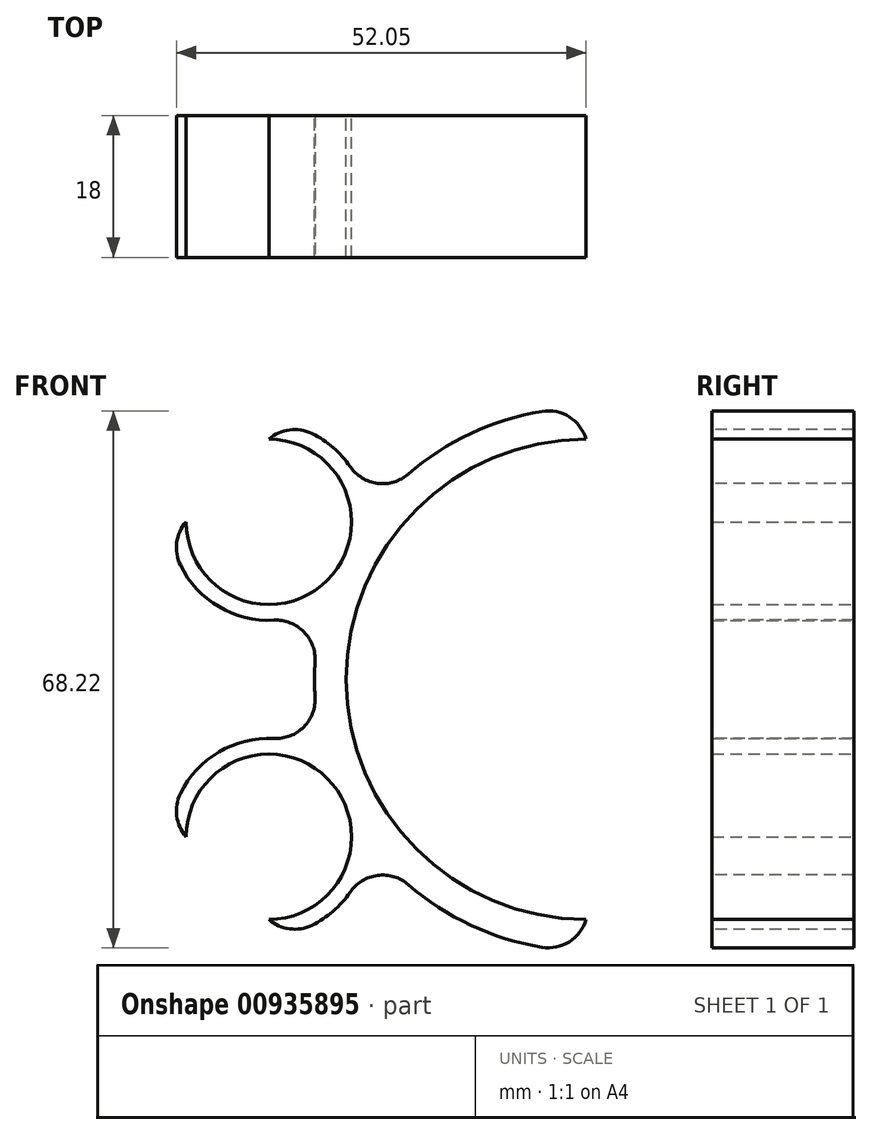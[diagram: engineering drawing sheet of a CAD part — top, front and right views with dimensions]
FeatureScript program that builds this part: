
annotation { "Feature Type Name" : "Feature", "Feature Type Description" : "" }
export const myFeature = defineFeature(function(context is Context, id is Id, definition is map)
    precondition{}
    {
        {
            var Q0;
            Q0=qCreatedBy(makeId("Front.planeOp"),FACE);
            var sketch = newSketch(context, id + "F0", { "sketchPlane" : qUnion([Q0])});
            skCircle(sketch, "E0", {"center": v(0, 0) * mm, "radius": 30.5 * mm});
            skCircle(sketch, "E1", {"center": v(0, 0) * mm, "radius": 34.5 * mm});
            skLineSegment(sketch, "E2", {"start": v(0, 73.77) * mm, "end": v(0, -63.44) * mm});
            skCircle(sketch, "E3", {"center": v(-40.31, 20) * mm, "radius": 10.5 * mm});
            skCircle(sketch, "E4.MirrorC", {"center": v(-40.31, -20) * mm, "radius": 10.5 * mm});
            skCircle(sketch, "E5.MirrorC", {"center": v(40.31, 20) * mm, "radius": 10.5 * mm});
            skCircle(sketch, "E6.MirrorC", {"center": v(40.31, -20) * mm, "radius": 10.5 * mm});
            skCircle(sketch, "E7", {"center": v(-40.31, 20) * mm, "radius": 12.5 * mm});
            skCircle(sketch, "E8.MirrorC", {"center": v(40.31, 20) * mm, "radius": 12.5 * mm});
            skCircle(sketch, "E9.MirrorC", {"center": v(-40.31, -20) * mm, "radius": 12.5 * mm});
            skCircle(sketch, "E10.MirrorC", {"center": v(40.31, -20) * mm, "radius": 12.5 * mm});
            skLineSegment(sketch, "E11", {"start": v(-40.31, 32.5) * mm, "end": v(-40.31, 20) * mm});
            skLineSegment(sketch, "E12", {"start": v(-52.81, 20) * mm, "end": v(-40.31, 20) * mm});
            skLineSegment(sketch, "E13.MirrorCS", {"start": v(-52.81, -20) * mm, "end": v(-40.31, -20) * mm});
            skLineSegment(sketch, "E14.MirrorCS", {"start": v(-40.31, -32.5) * mm, "end": v(-40.31, -20) * mm});
            skLineSegment(sketch, "E15.MirrorCS", {"start": v(40.31, 32.5) * mm, "end": v(40.31, 20) * mm});
            skLineSegment(sketch, "E16.MirrorCS", {"start": v(52.81, 20) * mm, "end": v(40.31, 20) * mm});
            skLineSegment(sketch, "E17.MirrorCS", {"start": v(40.31, -32.5) * mm, "end": v(40.31, -20) * mm});
            skLineSegment(sketch, "E18.MirrorCS", {"start": v(52.81, -20) * mm, "end": v(40.31, -20) * mm});
            skSolve(sketch);
        }
        {
            var Q0;
            {var subQ0=sQuery(id+"F0.wireOp",EDGE,"E7");var subQ1=sQuery(id+"F0.wireOp",EDGE,"E1");var subQ2=makeQuery(id+"F0.imprint","INTERSECT",VERTEX,{"disambiguationData":[OD(0.0)],"derivedFrom":[subQ1,subQ0]});Q0=makeQuery(id+"F0.imprint","IMPRINT",FACE,{"disambiguationData":[TD([[makeQuery(id+"F0.imprint","IMPRINT",EDGE,{"disambiguationData":[TD([[subQ2,-1.0]])],"derivedFrom":subQ1}),-1.0]])]});}
            var Q1;
            {var subQ0=sQuery(id+"F0.wireOp",EDGE,"E2");var subQ5=sQuery(id+"F0.wireOp",EDGE,"E0");var subQ6=makeQuery(id+"F0.imprint","INTERSECT",VERTEX,{"disambiguationData":[OD(0.0)],"derivedFrom":[subQ5,subQ0]});Q1=makeQuery(id+"F0.imprint","IMPRINT",FACE,{"disambiguationData":[TD([[makeQuery(id+"F0.imprint","IMPRINT",EDGE,{"disambiguationData":[TD([[subQ6,-1.0]])],"derivedFrom":subQ5}),-1.0]])]});}
            var Q2;
            {var subQ0=sQuery(id+"F0.wireOp",EDGE,"E7");var subQ1=sQuery(id+"F0.wireOp",EDGE,"E1");var subQ2=makeQuery(id+"F0.imprint","INTERSECT",VERTEX,{"disambiguationData":[OD(0.0)],"derivedFrom":[subQ1,subQ0]});Q2=makeQuery(id+"F0.imprint","IMPRINT",FACE,{"disambiguationData":[TD([[makeQuery(id+"F0.imprint","IMPRINT",EDGE,{"disambiguationData":[TD([[subQ2,-1.0]])],"derivedFrom":subQ1}),1.0]])]});}
            var Q3;
            {var subQ0=sQuery(id+"F0.wireOp",EDGE,"E9.MirrorC");var subQ1=sQuery(id+"F0.wireOp",EDGE,"E1");var subQ2=makeQuery(id+"F0.imprint","INTERSECT",VERTEX,{"disambiguationData":[OD(0.0)],"derivedFrom":[subQ1,subQ0]});Q3=makeQuery(id+"F0.imprint","IMPRINT",FACE,{"disambiguationData":[TD([[makeQuery(id+"F0.imprint","IMPRINT",EDGE,{"disambiguationData":[TD([[subQ2,-1.0]])],"derivedFrom":subQ1}),1.0]])]});}
            var Q4;
            {var subQ0=sQuery(id+"F0.wireOp",EDGE,"E7");var subQ1=sQuery(id+"F0.wireOp",EDGE,"E1");var subQ2=makeQuery(id+"F0.imprint","INTERSECT",VERTEX,{"disambiguationData":[OD(1.0)],"derivedFrom":[subQ1,subQ0]});Q4=makeQuery(id+"F0.imprint","IMPRINT",FACE,{"disambiguationData":[TD([[makeQuery(id+"F0.imprint","IMPRINT",EDGE,{"disambiguationData":[TD([[subQ2,1.0]])],"derivedFrom":subQ1}),-1.0]])]});}
            var Q5;
            {var subQ0=sQuery(id+"F0.wireOp",EDGE,"E9.MirrorC");var subQ1=sQuery(id+"F0.wireOp",EDGE,"E1");var subQ2=makeQuery(id+"F0.imprint","INTERSECT",VERTEX,{"disambiguationData":[OD(0.0)],"derivedFrom":[subQ1,subQ0]});Q5=makeQuery(id+"F0.imprint","IMPRINT",FACE,{"disambiguationData":[TD([[makeQuery(id+"F0.imprint","IMPRINT",EDGE,{"disambiguationData":[TD([[subQ2,-1.0]])],"derivedFrom":subQ1}),-1.0]])]});}
            var Q6;
            {var subQ0=sQuery(id+"F0.wireOp",EDGE,"E9.MirrorC");var subQ1=sQuery(id+"F0.wireOp",EDGE,"E1");var subQ2=makeQuery(id+"F0.imprint","INTERSECT",VERTEX,{"disambiguationData":[OD(1.0)],"derivedFrom":[subQ1,subQ0]});Q6=makeQuery(id+"F0.imprint","IMPRINT",FACE,{"disambiguationData":[TD([[makeQuery(id+"F0.imprint","IMPRINT",EDGE,{"disambiguationData":[TD([[subQ2,1.0]])],"derivedFrom":subQ1}),-1.0]])]});}
            extrude(context, id + "F1", {"entities" : qUnion([Q0, Q1, Q2, Q3, Q4, Q5, Q6]), "depth" : 18 * mm, "offsetDistance" : 25 * mm});
        }
        {
            var Q0;
            {var subQ0=sQuery(id+"F0.wireOp",EDGE,"E9.MirrorC");var subQ1=sQuery(id+"F0.wireOp",EDGE,"E1");Q0=makeQuery(id+"F1.opExtrude","SWEPT_EDGE",EDGE,{"disambiguationData":[OSD([subQ1,subQ0]),TDD([makeQuery(id+"F0.imprint","INTERSECT",VERTEX,{"disambiguationData":[OD(0.0)],"derivedFrom":[subQ1,subQ0]})])]});}
            var Q1;
            {var subQ0=sQuery(id+"F0.wireOp",EDGE,"E7");var subQ1=sQuery(id+"F0.wireOp",EDGE,"E1");Q1=makeQuery(id+"F1.opExtrude","SWEPT_EDGE",EDGE,{"disambiguationData":[OSD([subQ1,subQ0]),TDD([makeQuery(id+"F0.imprint","INTERSECT",VERTEX,{"disambiguationData":[OD(0.0)],"derivedFrom":[subQ1,subQ0]})])]});}
            var Q2;
            {var subQ0=sQuery(id+"F0.wireOp",EDGE,"E9.MirrorC");var subQ1=sQuery(id+"F0.wireOp",EDGE,"E1");Q2=makeQuery(id+"F1.opExtrude","SWEPT_EDGE",EDGE,{"disambiguationData":[OSD([subQ1,subQ0]),TDD([makeQuery(id+"F0.imprint","INTERSECT",VERTEX,{"disambiguationData":[OD(1.0)],"derivedFrom":[subQ1,subQ0]})])]});}
            var Q3;
            {var subQ0=sQuery(id+"F0.wireOp",EDGE,"E7");var subQ1=sQuery(id+"F0.wireOp",EDGE,"E1");Q3=makeQuery(id+"F1.opExtrude","SWEPT_EDGE",EDGE,{"disambiguationData":[OSD([subQ1,subQ0]),TDD([makeQuery(id+"F0.imprint","INTERSECT",VERTEX,{"disambiguationData":[OD(1.0)],"derivedFrom":[subQ1,subQ0]})])]});}
            var Q4;
            Q4=makeQuery(id+"F1.opExtrude","SWEPT_EDGE",EDGE,{"disambiguationData":[OSD([sQuery(id+"F0.wireOp",EDGE,"E7"),sQuery(id+"F0.wireOp",EDGE,"E11")])]});
            var Q5;
            Q5=makeQuery(id+"F1.opExtrude","SWEPT_EDGE",EDGE,{"disambiguationData":[OSD([sQuery(id+"F0.wireOp",EDGE,"E7"),sQuery(id+"F0.wireOp",EDGE,"E12")])]});
            var Q6;
            Q6=makeQuery(id+"F1.opExtrude","SWEPT_EDGE",EDGE,{"disambiguationData":[OSD([sQuery(id+"F0.wireOp",EDGE,"E9.MirrorC"),sQuery(id+"F0.wireOp",EDGE,"E13.MirrorCS")])]});
            var Q7;
            Q7=makeQuery(id+"F1.opExtrude","SWEPT_EDGE",EDGE,{"disambiguationData":[OSD([sQuery(id+"F0.wireOp",EDGE,"E9.MirrorC"),sQuery(id+"F0.wireOp",EDGE,"E14.MirrorCS")])]});
            var Q8;
            {var subQ0=sQuery(id+"F0.wireOp",EDGE,"E2");var subQ1=sQuery(id+"F0.wireOp",EDGE,"E1");Q8=makeQuery(id+"F1.opExtrude","SWEPT_EDGE",EDGE,{"disambiguationData":[OSD([subQ1,subQ0]),TDD([makeQuery(id+"F0.imprint","INTERSECT",VERTEX,{"disambiguationData":[OD(0.0)],"derivedFrom":[subQ1,subQ0]})])]});}
            var Q9;
            {var subQ0=sQuery(id+"F0.wireOp",EDGE,"E2");var subQ1=sQuery(id+"F0.wireOp",EDGE,"E1");Q9=makeQuery(id+"F1.opExtrude","SWEPT_EDGE",EDGE,{"disambiguationData":[OSD([subQ1,subQ0]),TDD([makeQuery(id+"F0.imprint","INTERSECT",VERTEX,{"disambiguationData":[OD(1.0)],"derivedFrom":[subQ1,subQ0]})])]});}
            fillet(context, id + "F2", {"entities" : qUnion([Q0, Q1, Q2, Q3, Q4, Q5, Q6, Q7, Q8, Q9]), "radius" : 5 * mm, "tangentPropagation" : true, "allowEdgeOverflow" : false});
        }
    });
